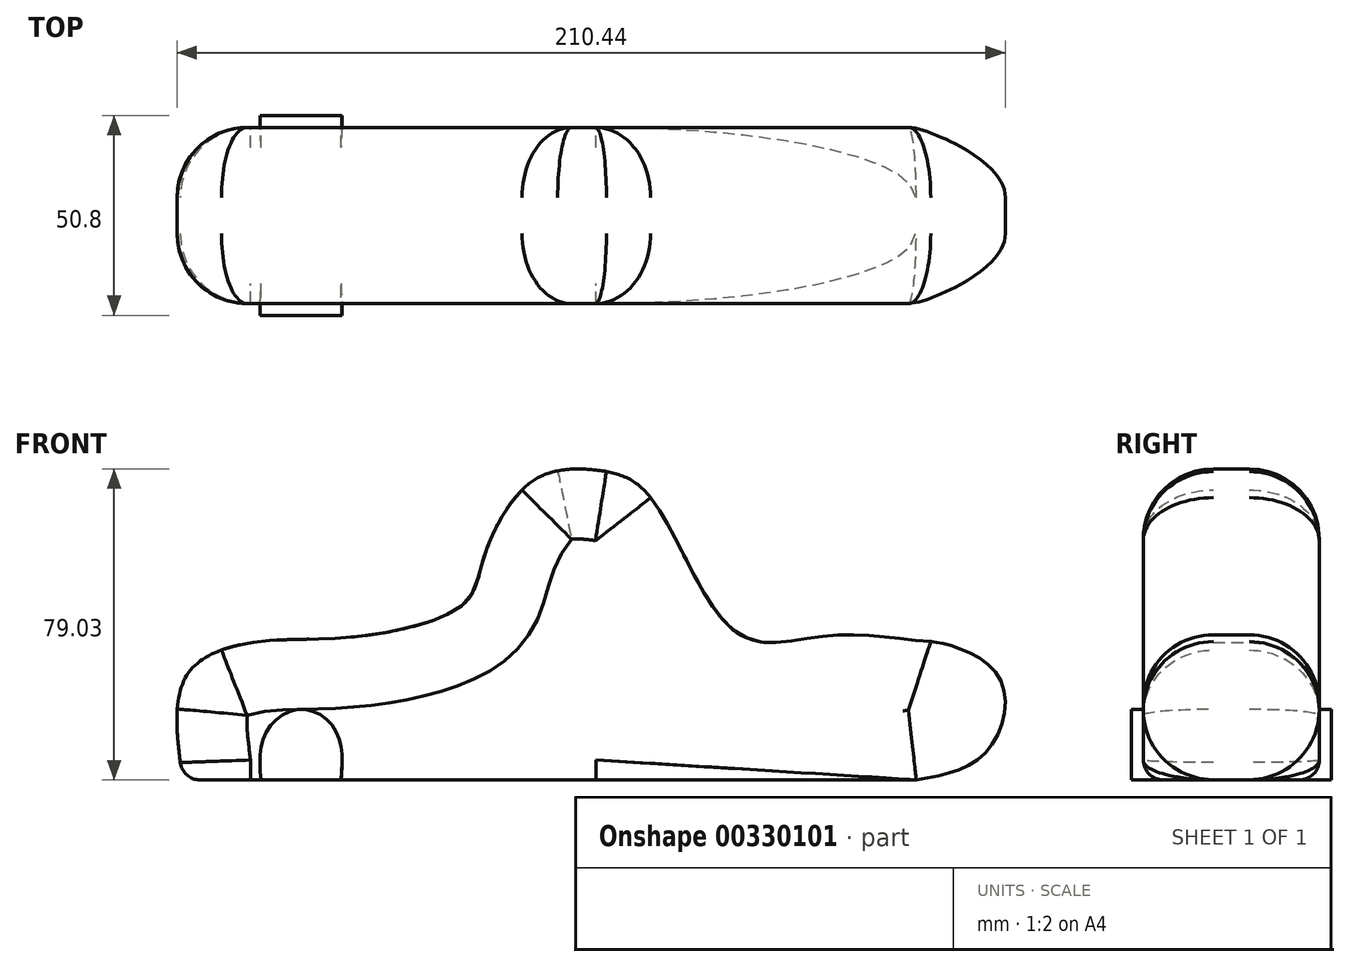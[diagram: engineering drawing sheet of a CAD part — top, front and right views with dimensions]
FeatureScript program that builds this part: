
annotation { "Feature Type Name" : "Feature", "Feature Type Description" : "" }
export const myFeature = defineFeature(function(context is Context, id is Id, definition is map)
    precondition{}
    {
        {
            var Q0;
            Q0=qCreatedBy(makeId("Front.planeOp"),FACE);
            var sketch = newSketch(context, id + "F0", { "sketchPlane" : qUnion([Q0])});
            skLineSegment(sketch, "E0", {"start": v(-76.48, 0) * mm, "end": v(76, 0) * mm});
            skLineSegment(sketch, "E1", {"start": v(-136.72, 0) * mm, "end": v(123.78, 0) * mm});
            skFitSpline(sketch, "E2", {"points": [v(109.36, 0) * mm, v(127.66, 7.1) * mm, v(130.99, 26.08) * mm, v(116.35, 34.73) * mm, v(110.36, 35.4) * mm, v(88.4, 36.73) * mm, v(64.43, 37.4) * mm, v(42.46, 71.67) * mm, v(29.15, 78.66) * mm, v(12.51, 76) * mm, v(0, 56.36) * mm, v(-5.13, 44.71) * mm, v(-32.75, 36.4) * mm, v(-57.7, 35.06) * mm, v(-75.35, 26.74) * mm, v(-76.48, 0) * mm], "startDerivative": vector(316.76, 50.7) * mm, "endDerivative": vector(55.22, -404.63) * mm});
            skSolve(sketch);
        }
        {
            var Q0;
            {var subQ0=sQuery(id+"F0.wireOp",EDGE,"E2");Q0=makeQuery(id+"F0.imprint","IMPRINT",FACE,{"disambiguationData":[TD([[makeQuery(id+"F0.imprint","IMPRINT",EDGE,{"derivedFrom":subQ0}),1.0]])]});}
            extrude(context, id + "F1", {"entities" : qUnion([Q0]), "endBound" : BoundingType.SYMMETRIC, "depth" : 44.7 * mm});
        }
        {
            var Q0;
            Q0=makeQuery(id+"F1.opExtrude","CAP_EDGE",EDGE,{"disambiguationData":[OSD([sQuery(id+"F0.wireOp",EDGE,"E2")])],"isStart":false});
            var Q1;
            Q1=makeQuery(id+"F1.opExtrude","CAP_EDGE",EDGE,{"disambiguationData":[OSD([sQuery(id+"F0.wireOp",EDGE,"E2")])],"isStart":true});
            fillet(context, id + "F2", {"entities" : qUnion([Q0, Q1]), "radius" : 17.78 * mm, "tangentPropagation" : true, "allowEdgeOverflow" : false});
        }
        {
            var Q0;
            Q0=makeQuery(id+"F2.opFillet","BLEND_EDGE",EDGE,{"disambiguationData":[OD(1.0)],"blendedFrom":[makeQuery(id+"F1.opExtrude","CAP_EDGE",EDGE,{"disambiguationData":[OSD([sQuery(id+"F0.wireOp",EDGE,"E2")])],"isStart":false}),makeQuery(id+"F1.opExtrude","SWEPT_FACE",FACE,{"disambiguationData":[OSD([sQuery(id+"F0.wireOp",EDGE,"E1")])]})],"blendedInto":[makeQuery(id+"F1.opExtrude","SWEPT_FACE",FACE,{"disambiguationData":[OSD([sQuery(id+"F0.wireOp",EDGE,"E1")])]})]});
            fillet(context, id + "F3", {"entities" : qUnion([Q0]), "radius" : 5.08 * mm, "tangentPropagation" : true, "allowEdgeOverflow" : false});
        }
        {
            var Q0;
            Q0=qCreatedBy(makeId("Front.planeOp"),FACE);
            var sketch = newSketch(context, id + "F4", { "sketchPlane" : qUnion([Q0])});
            skFitSpline(sketch, "E3", {"points": [v(-56.6, 0) * mm, v(-55.4, 11.96) * mm, v(-46.28, 17.95) * mm, v(-37.42, 12.2) * mm, v(-36.22, 0) * mm], "startDerivative": vector(-3.73, 49.56) * mm, "endDerivative": vector(-3.69, -50.39) * mm});
            skLineSegment(sketch, "E4", {"start": v(-56.6, 0) * mm, "end": v(-36.22, 0) * mm});
            skSolve(sketch);
        }
        {
            var Q0;
            Q0 = qSketchRegion(id + "F4", true);
            extrude(context, id + "F5", {"entities" : qUnion([Q0]), "operationType" : NewBodyOperationType.ADD, "endBound" : BoundingType.SYMMETRIC, "depth" : 50.8 * mm});
        }
    });
